# Revit family: Combina D 3.0
name_source: partatom
category: Lighting Fixtures
units: mm (PartAtom-declared; Revit-internal decimal feet)

## family parameters
Cut with Voids When Loaded = Yes
Host = Face
Light Source = Yes
Part Type = Normal
Room Calculation Point = Yes
Round Connector Dimension = Use Diameter
Shared = No

## types (12) — shared parameters
Apparent Load = 0 VA
Apparent Load Phase 1 = 15 W
Body = L&L_Anodized aluminium
CRI = CRI >90, CRI >97
Code = -
Color Filter = 16777215
Control system = ON/OFF
Cutout dimensions = diam. 136 mm
Default Elevation = 1219 mm
Delivered lumen output = 1094 lm (3000K, 400mA, 36°, CRI >97), 1177 lm (3000K, 400mA, 36°, CRI >90)
Description = Recessed downlight for indoor applications
Dimming Lamp Color Temperature Shift = <None>
Emit from Line Length = 610 mm
Energy efficiency class = A A+ A++
Features = UGR <13 for versions with flat and shallow covers, UGR <19 for versions with deep cover
Geometry = Combina D 3.0_mod
Height Void = 139 mm
Height mm = 135 mm  [stored 0.442913 ft]
IP = IP40, IP44 with filter
LED Colour = 3000K (also available: 2700K and 4000K - ref. URL Technical sheet)
Length mm = 136 mm
Lens = L&L_Tempered extra-clear glass
Lumen output at source = 1188 lm (3000K, 400mA, CRI >97), 1349 lm (3000K, 400mA, CRI >90)
Manufacturer = L&L Luce&Light
Material = body in die-cast aluminium and Bayblend, bezel and cover in die-cast aluminium
Model = Combina D 3.0
Mounting = recessed (ceiling)
No. and type of led = 1 power LED High Intensity, 2-step MacAdam, 50 000h L90 B10 (Ta 25°C)
Notes = -
Power = max 15W
Power cables = includes 2x0.30 m single-core PVC cables
Power supply = max 400mA
max 500mA
max 500mA
Power supply unit = not included
Radius Void = 50 mm  [stored 0.164042 ft]
Tilt Angle = 90.00°
Tiltable = -
Trim = L&L _Aluminium low copper
URL = https://www.lucelight.it
URL Accessories and power supply units = https://www.lucelight.it
URL Catalogue = https://www.lucelight.it
URL DXF = https://www.lucelight.it
URL Description = https://www.lucelight.it
URL General code = https://www.lucelight.it
URL IES Photometric file = https://www.lucelight.it
URL Image = https://www.lucelight.it
Voltage = 400 V
Weight kg = 0.90 kg
Width mm = 136 mm
Wiring = series

## per-type parameters (varying)
| type | Optics | Photometric Web File | Round Deep | Round Flat | Square Deep | Square Flat |
| COMBINA D 3.0 + CC3010 S 18° (3000K 15W 400mA)_Round Flat | 18° | COMBINA D 3.0 + CC3010 S 18° [3000K 15W 400mA].IES | No | Yes | No | No |
| COMBINA D 3.0 + CC3020 S 18° (3000K 15W 400mA)_Square Flat | 18° | COMBINA D 3.0 + CC3020 S 18° [3000K 15W 400mA].IES | No | No | No | Yes |
| COMBINA D 3.0 + CC3050 S 18° (3000K 15W 400mA)_Round Deep | 18° | COMBINA D 3.0 + CC3050 S 18° [3000K 15W 400mA].IES | Yes | No | No | No |
| COMBINA D 3.0 + CC3060 S 18° (3000K 15W 400mA)_Square Deep | 18° | COMBINA D 3.0 + CC3060 S 18° [3000K 15W 400mA].IES | No | No | Yes | No |
| COMBINA D 3.0 + CC3010 M 29° (3000K 15W 400mA)_Round Flat | 29° | COMBINA D 3.0 + CC3010 M 29° [3000K 15W 400mA].IES | No | Yes | No | No |
| COMBINA D 3.0 + CC3020 M 29° (3000K 15W 400mA)_Square Flat | 29° | COMBINA D 3.0 + CC3020 M 29° [3000K 15W 400mA].IES | No | No | No | Yes |
| COMBINA D 3.0 + CC3050 M 29° (3000K 15W 400mA)_Round Deep | 29° | COMBINA D 3.0 + CC3050 M 29° [3000K 15W 400mA].IES | Yes | No | No | No |
| COMBINA D 3.0 + CC3060 M 29° (3000K 15W 400mA)_Square Deep | 29° | COMBINA D 3.0 + CC3060 M 29° [3000K 15W 400mA].IES | No | No | Yes | No |
| COMBINA D 3.0 + CC3010 L 36° (3000K 15W 400mA)_Round Flat | 36° | COMBINA D 3.0 + CC3010 L 36° [3000K 15W 400mA].IES | No | Yes | No | No |
| COMBINA D 3.0 + CC3020 L 36° (3000K 15W 400mA)_Square Flat | 36° | COMBINA D 3.0 + CC3020 L 36° [3000K 15W 400mA].IES | No | No | No | Yes |
| COMBINA D 3.0 + CC3050 L 36° (3000K 15W 400mA)_Round Deep | 36° | COMBINA D 3.0 + CC3050 L 36° [3000K 15W 400mA].IES | Yes | No | No | No |
| COMBINA D 3.0 + CC3060 L 36° (3000K 15W 400mA)_Square Deep | 36° | COMBINA D 3.0 + CC3060 L 36° [3000K 15W 400mA].IES | No | No | Yes | No |

note: [stored X ft] marks values corroborated as IEEE doubles in the binary element streams (Revit-internal decimal feet)

## geometry (parser evidence)
native form markers: Blend x2, Sweep x6
no freeform markers — native parametric forms only
